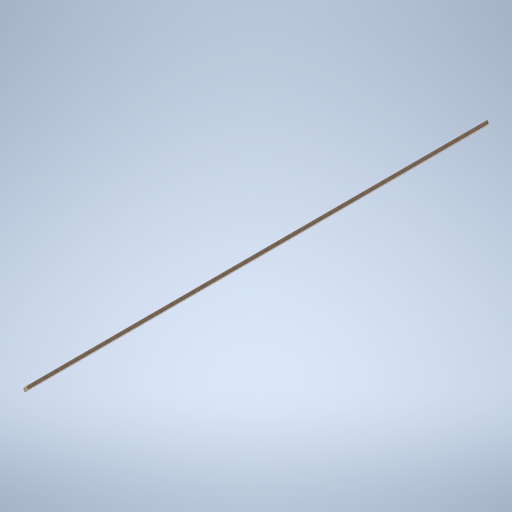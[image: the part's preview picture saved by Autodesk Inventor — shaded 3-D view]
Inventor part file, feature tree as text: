
AUTODESK INVENTOR PART (.ipt)
format: ipt  version: 2024.2 (Build 282272000, 272)  size: 272,896 bytes
history: native  units: mm
features: extrude x1, fillet x1, sketch x1
ambient origin geometry x8: Origin, YZ Plane, XZ Plane, XY Plane, X Axis, Y Axis, Z Axis, Center Point
bodies: Body1 (feature_tree)
feature tree (3):
  extrude  "Extrusion3"  Depth=800.0mm
  fillet  "Fillet2"  Radius=20000.0mm
  sketch  "Sketch2"  dims[d5=8500.0mm d20=800.0mm d21=20000.0mm d22=20000.0mm d23=0.0mm d24=0.0mm d25=50.0mm]
